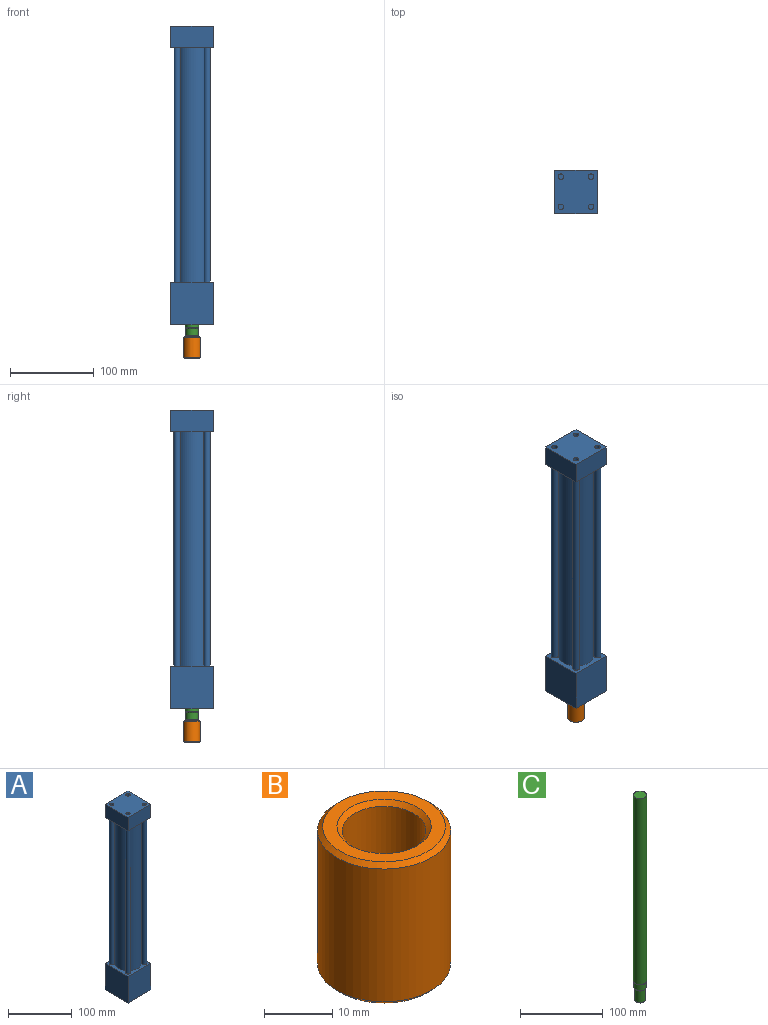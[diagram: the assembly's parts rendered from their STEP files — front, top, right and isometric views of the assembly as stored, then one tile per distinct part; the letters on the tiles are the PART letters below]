
ASSEMBLY  parts=3 mates=4
PART A: 39 faces, bbox 50.8x50.8x355.6 mm
  f0: cylinder r=20.64mm len=279.4mm, axis (0,0,-1), area 36229.6mm2, adj f10,f16
  f1: cylinder r=3.96mm len=279.4mm, axis (0,0,-1), area 6956.1mm2, adj f10,f16
  f2: cylinder r=3.96mm len=279.4mm, axis (0,0,-1), area 6956.1mm2, adj f10,f16
  f3: cylinder r=3.96mm len=279.4mm, axis (0,0,-1), area 6956.1mm2, adj f10,f16
  f4: cylinder r=3.96mm len=279.4mm, axis (0,0,-1), area 6956.1mm2, adj f10,f16
  f5: plane 50.8x25.4mm, normal (-1,0,0), area 1290.3mm2, adj f6,f8,f9,f10
  f6: plane 50.8x25.4mm, normal (0,-1,0), area 1290.3mm2, adj f5,f7,f9,f10
  f7: plane 50.8x25.4mm, normal (1,0,0), area 1290.3mm2, adj f6,f8,f9,f10
  f8: plane 50.8x25.4mm, normal (0,1,0), area 1187.7mm2, adj f5,f7,f9,f10,f37
  f9: plane 50.8x50.8mm, normal (0,0,1), area 2443.6mm2, adj f5,f6,f7,f8,f25,f27,f29,f31
  f10: plane 50.8x50.8mm, normal (0,0,-1), area 1045.3mm2, adj f0,f1,f2,f3,f4,f5,f6,f7
  f11: plane 50.8x50.8mm, normal (-1,0,0), area 2580.6mm2, adj f12,f14,f15,f16
  f12: plane 50.8x50.8mm, normal (0,1,0), area 2478mm2, adj f11,f13,f15,f16,f35
  f13: plane 50.8x50.8mm, normal (1,0,0), area 2580.6mm2, adj f12,f14,f15,f16
  f14: plane 50.8x50.8mm, normal (0,-1,0), area 2580.6mm2, adj f11,f13,f15,f16
  f15: plane 50.8x50.8mm, normal (0,0,-1), area 1651.9mm2, adj f11,f12,f13,f14,f17,f19,f21,f23
  f16: plane 50.8x50.8mm, normal (0,0,1), area 1045.3mm2, adj f0,f1,f2,f3,f4,f11,f12,f13
  f17: cylinder r=3.3mm len=17.78mm, axis (0,0,-1), area 368.9mm2, adj f15,f18
  f18: plane 6.6x6.6mm, normal (0,0,-1), area 34.3mm2, adj f17
  f19: cylinder r=3.3mm len=17.78mm, axis (0,0,-1), area 368.9mm2, adj f15,f20
  f20: plane 6.6x6.6mm, normal (0,0,-1), area 34.3mm2, adj f19
  f21: cylinder r=3.3mm len=17.78mm, axis (0,0,-1), area 368.9mm2, adj f15,f22
  f22: plane 6.6x6.6mm, normal (0,0,-1), area 34.3mm2, adj f21
  f23: cylinder r=3.3mm len=17.78mm, axis (0,0,-1), area 368.9mm2, adj f15,f24
  f24: plane 6.6x6.6mm, normal (0,0,-1), area 34.3mm2, adj f23
  f25: cylinder r=3.3mm len=17.78mm, axis (0,0,1), area 368.9mm2, adj f9,f26
  f26: plane 6.6x6.6mm, normal (0,0,1), area 34.3mm2, adj f25
  f27: cylinder r=3.3mm len=17.78mm, axis (0,0,1), area 368.9mm2, adj f9,f28
  f28: plane 6.6x6.6mm, normal (0,0,1), area 34.3mm2, adj f27
  f29: cylinder r=3.3mm len=17.78mm, axis (0,0,1), area 368.9mm2, adj f9,f30
  f30: plane 6.6x6.6mm, normal (0,0,1), area 34.3mm2, adj f29
  f31: cylinder r=3.3mm len=17.78mm, axis (0,0,1), area 368.9mm2, adj f9,f32
  f32: plane 6.6x6.6mm, normal (0,0,1), area 34.3mm2, adj f31
  f33: cylinder r=15.88mm len=31.75mm, axis (0,0,-1), area 316.7mm2, adj f15,f34
  f34: plane 31.75x31.75mm, normal (0,0,-1), area 791.7mm2, adj f33
  f35: cylinder r=5.71mm len=12.7mm, axis (0,1,0), area 456mm2, adj f12,f36
  f36: plane 11.43x11.43mm, normal (0,1,0), area 102.6mm2, adj f35
  f37: cylinder r=5.71mm len=12.7mm, axis (0,1,0), area 456mm2, adj f8,f38
  f38: plane 11.43x11.43mm, normal (0,1,0), area 102.6mm2, adj f37
PART B: 8 faces, bbox 19.6x19.6x25.4 mm
  f0: cylinder r=9.78mm len=23.88mm, axis (0,0,-1), area 1467mm2, adj f3,f7
  f1: plane 18.03x18.03mm, normal (0,0,1), area 104.9mm2, adj f6,f7
  f2: plane 18.03x18.03mm, normal (0,0,-1), area 255.4mm2, adj f3
  f3: cone r=9.78mm half-angle=45deg, axis (0,0,1), area 63.6mm2, adj f0,f2
  f4: cylinder r=6.16mm len=18.29mm, axis (0,0,1), area 707.8mm2, adj f5,f6
  f5: plane 12.32x12.32mm, normal (0,0,1), area 119.2mm2, adj f4
  f6: cone r=6.16mm half-angle=45deg, axis (0,0,1), area 44.3mm2, adj f1,f4
  f7: cone r=9.02mm half-angle=45deg, axis (0,0,-1), area 63.6mm2, adj f0,f1
PART C: 9 faces, bbox 17.2x17.2x304.8 mm
  f0: cylinder r=7.49mm len=14.99mm, axis (0,0,-1), area 400.6mm2, adj f7,f8
  f1: cylinder r=7.94mm len=275.39mm, axis (0,0,-1), area 13734.2mm2, adj f2,f8
  f2: plane 15.88x15.88mm, normal (0,0,1), area 197.9mm2, adj f1
  f3: cylinder r=6.22mm len=17.78mm, axis (0,0,-1), area 695.2mm2, adj f4,f6
  f4: plane 12.95x12.95mm, normal (0,0,-1), area 10.1mm2, adj f3,f7
  f5: plane 9.91x9.91mm, normal (0,0,-1), area 77.1mm2, adj f6
  f6: cone r=4.95mm half-angle=45deg, axis (0,0,1), area 63.1mm2, adj f3,f5
  f7: torus R=6.48mm, axis (0,0,-1), area 71.4mm2, adj f0,f4
  f8: torus R=6.92mm, axis (0,0,-1), area 48.4mm2, adj f0,f1
PLACE A at identity fixed
PLACE B rot(axis=(0,0,1),90deg) t=(0,0,-90.49)mm
PLACE C rot(axis=(0,0,1),0deg) t=(0,0,-84.14)mm
MATE cylindrical C.f0 <-> B.f0  axis (0,0,-1) through (0,0,-73.98)mm
MATE cylindrical C.f0 <-> A.f0  axis (0,0,-1) through (0,0,82.97)mm
MATE planar B.f0 <-> C.f0  axis (0,0,1) through (0,0,-84.14)mm
MATE slider C.f0 <-> A.f0  axis (0,0,-1) through (0,0,-84.14)mm
